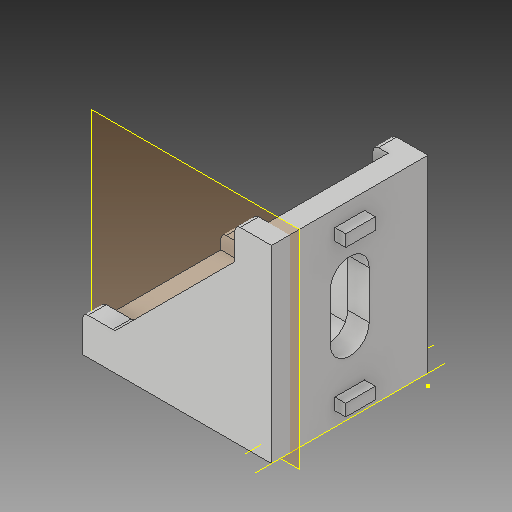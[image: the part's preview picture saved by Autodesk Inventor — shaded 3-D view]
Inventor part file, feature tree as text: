
AUTODESK INVENTOR PART (.ipt)
format: ipt  version: 2018 (Build 220112000, 112)  size: 218,112 bytes
history: native  units: mm
features: sketch x8, extrude x5, other x2, plane x1, fillet x1, pattern_circular x1, projected_geometry x1
ambient origin geometry x8: Origin, YZ Plane, XZ Plane, XY Plane, X Axis, Y Axis, Z Axis, Center Point
bodies: Solid1 (feature_tree)
feature tree (19):
  extrude  "Extrusion1"  Depth=6.8mm
  plane  "Work Plane1"
  extrude  "Extrusion2"  Depth=6.0mm
  extrude  "Extrusion3"  TaperAngle=180.0deg  [1 undecoded]
  fillet  "Fillet1"  Radius=6.8mm
  sketch  "Sketch4"  dims[d7=6.0mm]
  other  "Work Axis1"
  pattern_circular  "Circular Pattern1"  [2 undecoded]
  extrude  "Extrusion4"  Depth=22.2mm TaperAngle=0.0deg
  other  "Work Axis2"
  sketch  "Sketch7"  dims[d9=1.0mm]
  extrude  "Extrusion5"  Depth=2.0mm
  sketch  "Sketch10"  dims[d12=-3.4mm d13=4.0mm d14=22.2mm d15=0.0mm d16=9.0mm d17=3.6mm d18=16.0mm d19=3.6mm d20=22.2mm d21=0.0mm d22=1.0mm d23=2.0mm d24=2.0mm d25=2.0mm d26=20.0mm d27=270.0deg d29=3.0mm d30=0.0mm d31=2.75mm d32=5.5mm d33=2.2mm d34=2.6mm d35=2.75mm d36=2.2mm d37=5.5mm d38=2.0mm d39=0.0mm d41=2.0mm d42=0.0mm]
  sketch  "Sketch1"  dims[d0=35.0mm d1=6.8mm]
  sketch  "Sketch2"  dims[d2=90.0deg d3=6.0mm]
  sketch  "Sketch3"  dims[d4=35.0mm d5=180.0deg d6=6.8mm]
  sketch  "Sketch5"  dims[d8=90.0deg]
  sketch  "Sketch9"  dims[d10=29.0mm d11=0.0mm]
  projected_geometry  "Projected Loop4"
note: 3 required parameter values undecoded (feature->parameter linkage not recoverable at this tier; creation-order binding heuristic only, values carry confidence <= 0.55)
